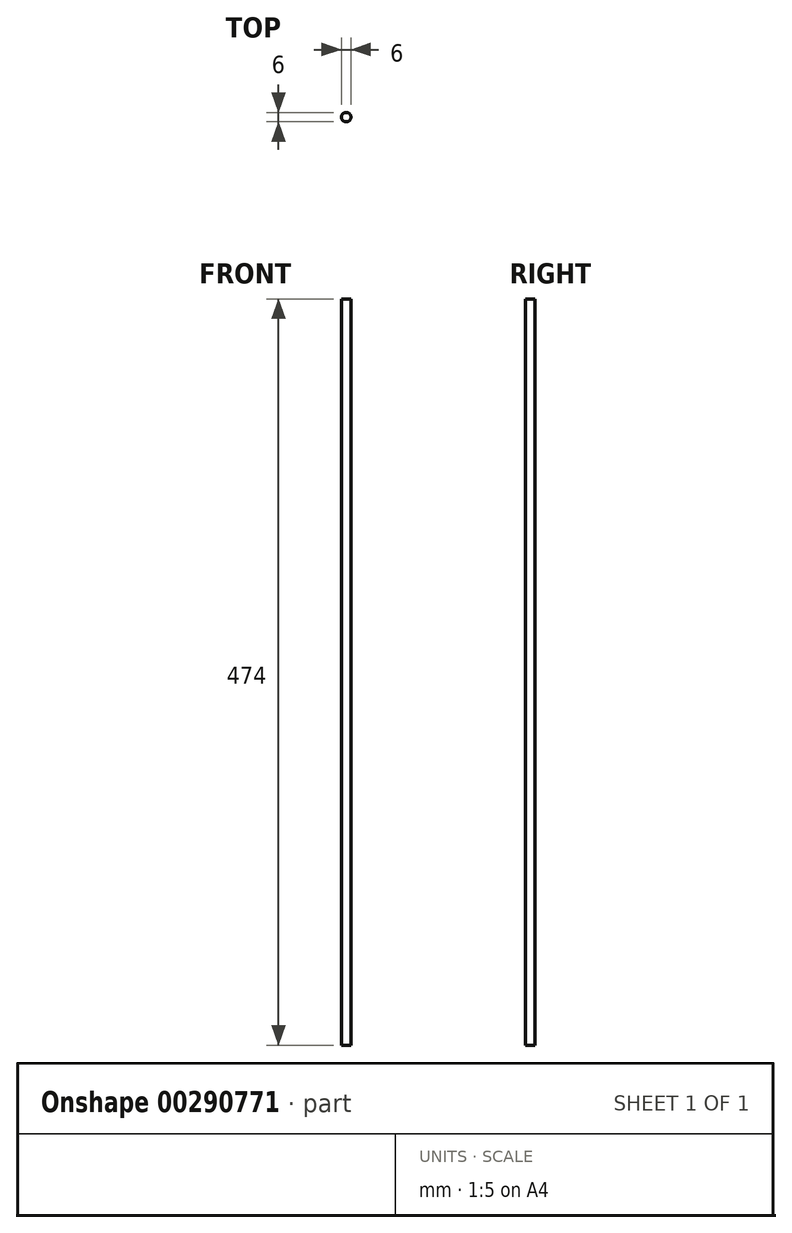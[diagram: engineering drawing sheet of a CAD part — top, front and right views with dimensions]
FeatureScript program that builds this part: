
annotation { "Feature Type Name" : "Feature", "Feature Type Description" : "" }
export const myFeature = defineFeature(function(context is Context, id is Id, definition is map)
    precondition{}
    {
        {
            var Q0;
            Q0=qCreatedBy(makeId("Top.planeOp"),FACE);
            var sketch = newSketch(context, id + "F0", { "sketchPlane" : qUnion([Q0])});
            skCircle(sketch, "E0", {"center": v(0, 0) * mm, "radius": 3 * mm});
            skSolve(sketch);
        }
        {
            var Q0;
            Q0 = qSketchRegion(id + "F0", true);
            extrude(context, id + "F1", {"entities" : qUnion([Q0]), "depth" : (158 * 3) * mm});
        }
    });
